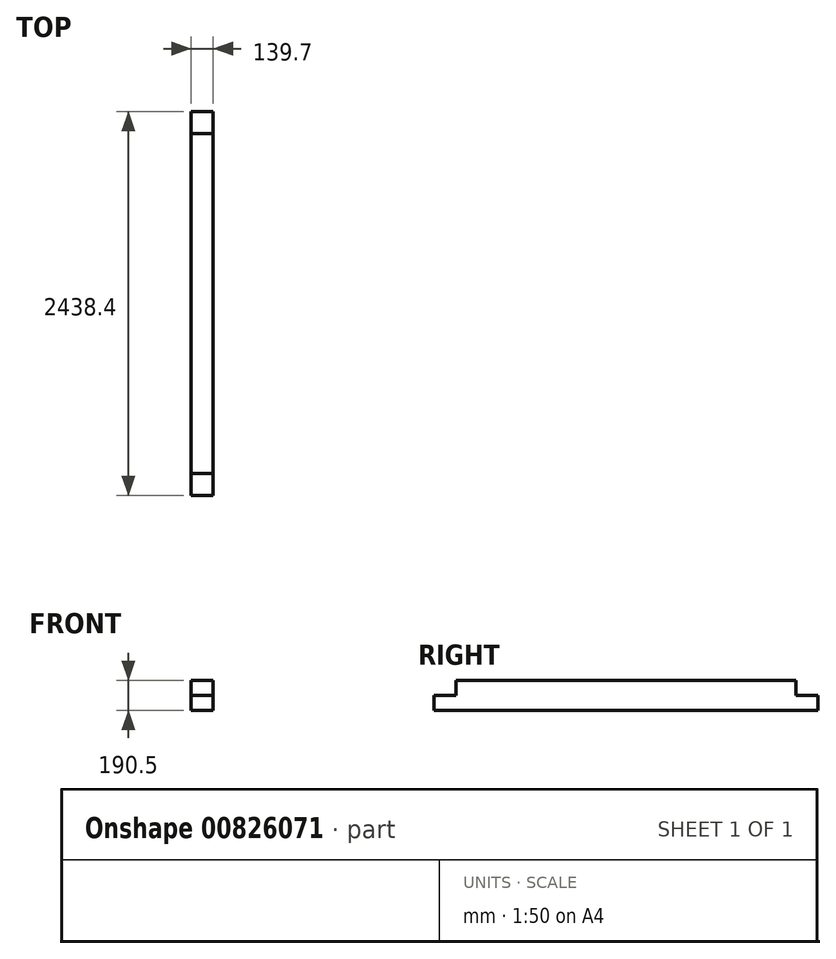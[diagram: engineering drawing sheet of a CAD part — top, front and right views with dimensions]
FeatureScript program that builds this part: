
annotation { "Feature Type Name" : "Feature", "Feature Type Description" : "" }
export const myFeature = defineFeature(function(context is Context, id is Id, definition is map)
    precondition{}
    {
        {
            var Q0;
            Q0=qCreatedBy(makeId("Right.planeOp"),FACE);
            var sketch = newSketch(context, id + "F0", { "sketchPlane" : qUnion([Q0])});
            skLineSegment(sketch, "E0.bottom", {"start": v(0, 0) * mm, "end": v(2438.4, 0) * mm});
            skLineSegment(sketch, "E0.top", {"start": v(0, 190.5) * mm, "end": v(2438.4, 190.5) * mm});
            skLineSegment(sketch, "E0.left", {"start": v(0, 0) * mm, "end": v(0, 190.5) * mm});
            skLineSegment(sketch, "E0.right", {"start": v(2438.4, 0) * mm, "end": v(2438.4, 190.5) * mm});
            skLineSegment(sketch, "E1.bottom", {"start": v(0, 190.5) * mm, "end": v(139.7, 190.5) * mm});
            skLineSegment(sketch, "E1.top", {"start": v(0, 95.25) * mm, "end": v(139.7, 95.25) * mm});
            skLineSegment(sketch, "E1.left", {"start": v(0, 190.5) * mm, "end": v(0, 95.25) * mm});
            skLineSegment(sketch, "E1.right", {"start": v(139.7, 190.5) * mm, "end": v(139.7, 95.25) * mm});
            skLineSegment(sketch, "E2.bottom", {"start": v(2298.7, 95.25) * mm, "end": v(2438.4, 95.25) * mm});
            skLineSegment(sketch, "E2.top", {"start": v(2298.7, 190.5) * mm, "end": v(2438.4, 190.5) * mm});
            skLineSegment(sketch, "E2.left", {"start": v(2298.7, 95.25) * mm, "end": v(2298.7, 190.5) * mm});
            skLineSegment(sketch, "E2.right", {"start": v(2438.4, 95.25) * mm, "end": v(2438.4, 190.5) * mm});
            skSolve(sketch);
        }
        {
            var Q0;
            Q0=makeQuery(id+"F0.imprint","IMPRINT",FACE,{"disambiguationData":[TD([[makeQuery(id+"F0.imprint","IMPRINT",EDGE,{"derivedFrom":sQuery(id+"F0.wireOp",EDGE,"E0.bottom")}),1.0]])]});
            extrude(context, id + "F1", {"entities" : qUnion([Q0]), "depth" : 139.7 * mm, "offsetDistance" : 25.4 * mm});
        }
    });
